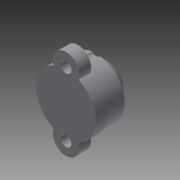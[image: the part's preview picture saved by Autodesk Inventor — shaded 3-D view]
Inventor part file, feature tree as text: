
AUTODESK INVENTOR PART (.ipt)
format: ipt  version: 2015 (Build 190159000, 159)  size: 163,840 bytes
history: native  units: mm
features: sketch x3, extrude x2, revolve x1
ambient origin geometry x8: Origin, YZ Plane, XZ Plane, XY Plane, X Axis, Y Axis, Z Axis, Center Point
bodies: Solid1 (feature_tree)
feature tree (6):
  extrude  "Extrusion1"  Depth=2.286mm
  extrude  "Extrusion2"  Depth=6.731mm
  revolve  "Revolution1"  [1 undecoded]
  sketch  "Sketch1"  dims[d0=12.7mm d1=2.286mm]
  sketch  "Sketch2"  dims[d2=2.286mm d3=6.731mm]
  sketch  "Sketch3"  dims[d4=6.731mm d5=13.462mm d6=19.05mm d7=2.54mm d8=0.0mm d9=3.81mm d10=0.0mm d11=10.16mm d12=10.16mm d13=90.0deg]
note: 1 required parameter value undecoded (feature->parameter linkage not recoverable at this tier; creation-order binding heuristic only, values carry confidence <= 0.55)
